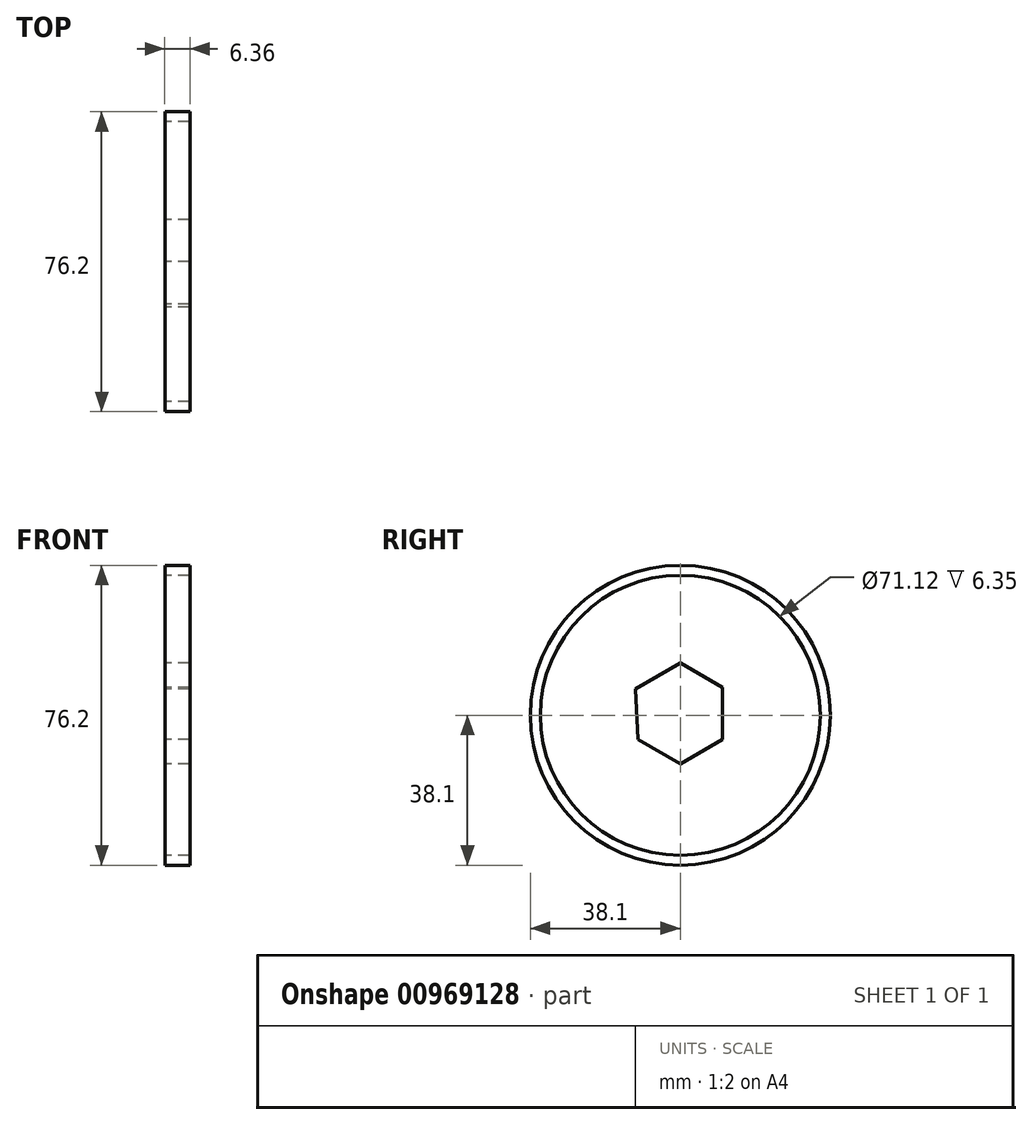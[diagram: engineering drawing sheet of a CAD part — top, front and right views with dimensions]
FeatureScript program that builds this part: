
annotation { "Feature Type Name" : "Feature", "Feature Type Description" : "" }
export const myFeature = defineFeature(function(context is Context, id is Id, definition is map)
    precondition{}
    {
        {
            var Q0;
            Q0=qCreatedBy(makeId("Right.planeOp"),FACE);
            var sketch = newSketch(context, id + "F0", { "sketchPlane" : qUnion([Q0])});
            skCircle(sketch, "E0", {"center": v(0, 0) * mm, "radius": 38.1 * mm});
            skCircle(sketch, "E1.cCircle", {"center": v(0, 0) * mm, "radius": 7.04 * mm, "construction": true});
            skLineSegment(sketch, "E1.0", {"start": v(6.1, 3.52) * mm, "end": v(6.1, -3.52) * mm});
            skLineSegment(sketch, "E1.1", {"start": v(6.1, -3.52) * mm, "end": v(0, -7.04) * mm});
            skLineSegment(sketch, "E1.2", {"start": v(0, -7.04) * mm, "end": v(-6.1, -3.52) * mm});
            skLineSegment(sketch, "E1.3", {"start": v(-6.1, -3.52) * mm, "end": v(-6.1, 3.52) * mm});
            skLineSegment(sketch, "E1.4", {"start": v(-6.1, 3.52) * mm, "end": v(0, 7.04) * mm});
            skLineSegment(sketch, "E1.5", {"start": v(0, 7.04) * mm, "end": v(6.1, 3.52) * mm});
            skPoint(sketch, "E2.startSnap0", {"position": v(3.05, 5.28) * mm});
            skCircle(sketch, "E3", {"center": v(0, 0) * mm, "radius": 35.56 * mm});
            skLineSegment(sketch, "E4", {"start": v(0, 7.04) * mm, "end": v(0, 33.94) * mm});
            skLineSegment(sketch, "E5", {"start": v(6.1, 3.52) * mm, "end": v(30.8, 17.78) * mm});
            skPoint(sketch, "E6.startSnap0", {"position": v(-3.05, -5.28) * mm});
            skPoint(sketch, "E7.startSnap0", {"position": v(-3.05, 5.28) * mm});
            skLineSegment(sketch, "E8", {"start": v(6.1, -3.52) * mm, "end": v(30.8, -17.78) * mm});
            skLineSegment(sketch, "E9", {"start": v(0, -7.04) * mm, "end": v(0, -35.56) * mm});
            skLineSegment(sketch, "E10", {"start": v(-6.1, -3.52) * mm, "end": v(-30.8, -17.78) * mm});
            skLineSegment(sketch, "E11", {"start": v(-6.1, 3.52) * mm, "end": v(-30.8, 17.78) * mm});
            skLineSegment(sketch, "E12", {"start": v(-11.46, 6.62) * mm, "end": v(0, 13.24) * mm});
            skLineSegment(sketch, "E13", {"start": v(0, 13.24) * mm, "end": v(10.74, 7.04) * mm});
            skLineSegment(sketch, "E14", {"start": v(10.74, 7.04) * mm, "end": v(10.74, -6.2) * mm});
            skLineSegment(sketch, "E15", {"start": v(10.74, -6.2) * mm, "end": v(0, -12.4) * mm});
            skLineSegment(sketch, "E16", {"start": v(-10.74, -6.2) * mm, "end": v(0, -12.4) * mm});
            skLineSegment(sketch, "E17", {"start": v(-11.46, 6.62) * mm, "end": v(-10.74, -6.2) * mm});
            skLineSegment(sketch, "E18", {"start": v(-29.09, 20.46) * mm, "end": v(-32.26, 14.96) * mm});
            skLineSegment(sketch, "E19", {"start": v(-8.3, 8.45) * mm, "end": v(-29.09, 20.46) * mm});
            skLineSegment(sketch, "E20", {"start": v(-32.26, 14.96) * mm, "end": v(-11.25, 2.83) * mm});
            skLineSegment(sketch, "E21", {"start": v(0, 33.94) * mm, "end": v(0, 35.56) * mm});
            skLineSegment(sketch, "E22", {"start": v(8.95, -7.23) * mm, "end": v(29.86, -19.3) * mm});
            skLineSegment(sketch, "E23", {"start": v(10.74, -3.58) * mm, "end": v(31.87, -15.78) * mm});
            skLineSegment(sketch, "E24", {"start": v(3.17, -10.57) * mm, "end": v(3.17, -35.42) * mm});
            skLineSegment(sketch, "E25", {"start": v(-2.26, -11.1) * mm, "end": v(-2.26, -35.49) * mm});
            skSolve(sketch);
        }
        {
            var Q0;
            Q0=makeQuery(id+"F0.imprint","IMPRINT",FACE,{"disambiguationData":[TD([[makeQuery(id+"F0.imprint","IMPRINT",EDGE,{"derivedFrom":sQuery(id+"F0.wireOp",EDGE,"E0")}),1.0]])]});
            var Q1;
            {var subQ0=sQuery(id+"F0.wireOp",EDGE,"E1.3");Q1=makeQuery(id+"F0.imprint","IMPRINT",FACE,{"disambiguationData":[TD([[makeQuery(id+"F0.imprint","IMPRINT",EDGE,{"derivedFrom":subQ0}),1.0]])]});}
            var Q2;
            {var subQ0=sQuery(id+"F0.wireOp",EDGE,"E1.4");Q2=makeQuery(id+"F0.imprint","IMPRINT",FACE,{"disambiguationData":[TD([[makeQuery(id+"F0.imprint","IMPRINT",EDGE,{"derivedFrom":subQ0}),1.0]])]});}
            var Q3;
            {var subQ2=sQuery(id+"F0.wireOp",EDGE,"E1.5");Q3=makeQuery(id+"F0.imprint","IMPRINT",FACE,{"disambiguationData":[TD([[makeQuery(id+"F0.imprint","IMPRINT",EDGE,{"derivedFrom":subQ2}),1.0]])]});}
            var Q4;
            {var subQ0=sQuery(id+"F0.wireOp",EDGE,"E1.0");Q4=makeQuery(id+"F0.imprint","IMPRINT",FACE,{"disambiguationData":[TD([[makeQuery(id+"F0.imprint","IMPRINT",EDGE,{"derivedFrom":subQ0}),1.0]])]});}
            var Q5;
            {var subQ0=sQuery(id+"F0.wireOp",EDGE,"E1.1");Q5=makeQuery(id+"F0.imprint","IMPRINT",FACE,{"disambiguationData":[TD([[makeQuery(id+"F0.imprint","IMPRINT",EDGE,{"derivedFrom":subQ0}),1.0]])]});}
            var Q6;
            {var subQ0=sQuery(id+"F0.wireOp",EDGE,"E1.2");Q6=makeQuery(id+"F0.imprint","IMPRINT",FACE,{"disambiguationData":[TD([[makeQuery(id+"F0.imprint","IMPRINT",EDGE,{"derivedFrom":subQ0}),1.0]])]});}
            var Q7;
            Q7=makeQuery(id+"F0.imprint","IMPRINT",FACE,{"disambiguationData":[TD([[makeQuery(id+"F0.imprint","IMPRINT",EDGE,{"derivedFrom":sQuery(id+"F0.wireOp",EDGE,"E1.0")}),-1.0]])]});
            extrude(context, id + "F1", {"entities" : qUnion([Q0, Q1, Q2, Q3, Q4, Q5, Q6, Q7]), "endBound" : BoundingType.SYMMETRIC, "depth" : 6.35 * mm, "offsetDistance" : 25.4 * mm});
        }
    });
